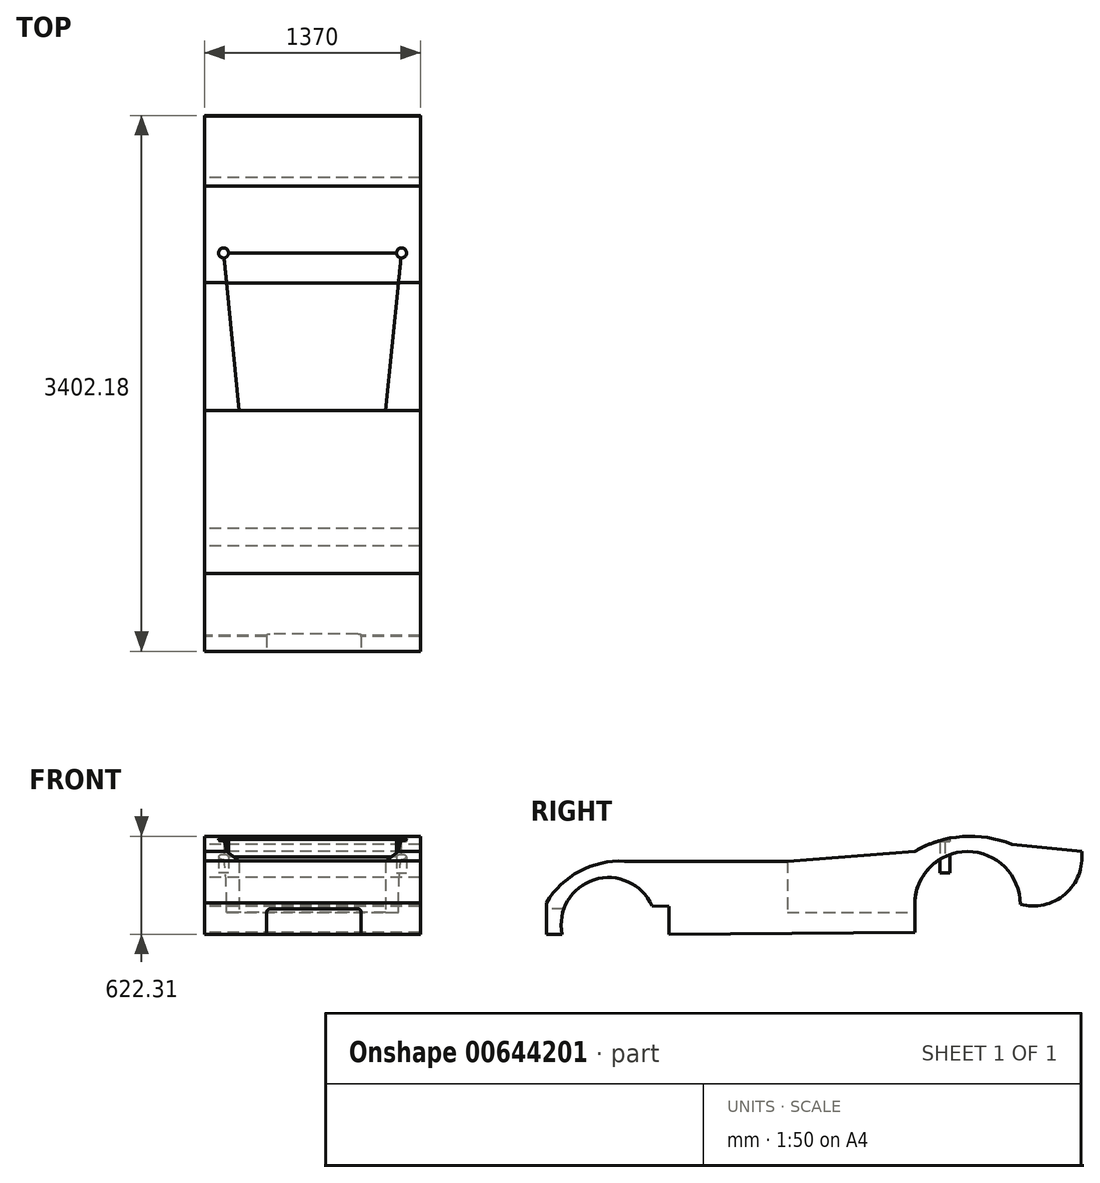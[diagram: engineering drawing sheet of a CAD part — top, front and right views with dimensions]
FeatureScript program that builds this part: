
annotation { "Feature Type Name" : "Feature", "Feature Type Description" : "" }
export const myFeature = defineFeature(function(context is Context, id is Id, definition is map)
    precondition{}
    {
        {
            var Q0;
            Q0=qCreatedBy(makeId("Right.planeOp"),FACE);
            var sketch = newSketch(context, id + "F0", { "sketchPlane" : qUnion([Q0])});
            skLineSegment(sketch, "E0", {"start": v(-1911.58, -464.58) * mm, "end": v(1488.42, -464.58) * mm, "construction": true});
            skLineSegment(sketch, "E1", {"start": v(1488.42, -464.58) * mm, "end": v(1488.42, 515.42) * mm, "construction": true});
            skLineSegment(sketch, "E2", {"start": v(-1911.58, -389.58) * mm, "end": v(-1811.58, -389.58) * mm});
            skLineSegment(sketch, "E3", {"start": v(-1131.58, -389.58) * mm, "end": v(428.38, -377.58) * mm});
            skLineSegment(sketch, "E4", {"start": v(-1131.58, -211.58) * mm, "end": v(428.38, -199.58) * mm});
            skLineSegment(sketch, "E5", {"start": v(428.38, -199.58) * mm, "end": v(428.38, -377.58) * mm});
            skLineSegment(sketch, "E6", {"start": v(-1131.58, -211.58) * mm, "end": v(-1131.58, -389.58) * mm});
            skArc(sketch, "E7", {"start": v(-1241.58, -209.76) * mm, "mid": v(-1607.46, -43.28) * mm, "end": v(-1811.58, -389.58) * mm});
            skLineSegment(sketch, "E8", {"start": v(-381.58, 74.2) * mm, "end": v(-1416.41, 74.2) * mm});
            skLineSegment(sketch, "E9", {"start": v(-1911.58, -389.58) * mm, "end": v(-1911.58, -189.58) * mm});
            skArc(sketch, "E10", {"start": v(-1416.41, 74.2) * mm, "mid": v(-1700.44, 10.73) * mm, "end": v(-1911.58, -189.58) * mm});
            skArc(sketch, "E11", {"start": v(1098.38, -199.58) * mm, "mid": v(763.38, 135.42) * mm, "end": v(428.38, -199.58) * mm});
            skLineSegment(sketch, "E12", {"start": v(-381.58, 74.2) * mm, "end": v(429.07, 137.05) * mm});
            skArc(sketch, "E13", {"start": v(1044.38, 181.8) * mm, "mid": v(731.52, 230.89) * mm, "end": v(429.07, 137.05) * mm});
            skArc(sketch, "E14", {"start": v(1098.38, -199.58) * mm, "mid": v(1382.86, -134.93) * mm, "end": v(1488.42, 137.05) * mm});
            skLineSegment(sketch, "E15", {"start": v(1488.42, 137.05) * mm, "end": v(1044.38, 181.8) * mm});
            skLineSegment(sketch, "E16", {"start": v(-1241.58, -209.76) * mm, "end": v(-1131.58, -211.58) * mm});
            skSolve(sketch);
        }
        {
            var Q0;
            Q0 = qSketchRegion(id + "F0", true);
            extrude(context, id + "F1", {"entities" : qUnion([Q0]), "depth" : 1370 * mm, "offsetDistance" : 25 * mm});
        }
        {
            var Q0;
            Q0=qCreatedBy(makeId("Top.planeOp"),FACE);
            var sketch = newSketch(context, id + "F2", { "sketchPlane" : qUnion([Q0])});
            skLineSegment(sketch, "E17", {"start": v(220, -381.58) * mm, "end": v(120, 618.42) * mm});
            skLineSegment(sketch, "E18", {"start": v(120, 618.42) * mm, "end": v(1250, 618.42) * mm});
            skLineSegment(sketch, "E19", {"start": v(1150, -381.58) * mm, "end": v(220, -381.58) * mm});
            skLineSegment(sketch, "E20", {"start": v(1150, -381.58) * mm, "end": v(1250, 618.42) * mm});
            skCircle(sketch, "E21", {"center": v(120, 618.42) * mm, "radius": 31.75 * mm});
            skCircle(sketch, "E22", {"center": v(1250, 618.42) * mm, "radius": 31.75 * mm});
            skSolve(sketch);
        }
        {
            var Q0;
            Q0 = qSketchRegion(id + "F2", true);
            extrude(context, id + "F3", {"entities" : qUnion([Q0]), "operationType" : NewBodyOperationType.REMOVE, "depth" : 350 * mm, "hasOffset" : true, "offsetDistance" : 200 * mm, "offsetOppositeDirection" : true, "hasSecondDirection" : true, "secondDirectionOppositeDirection" : true, "secondDirectionDepth" : 250 * mm});
        }
        {
            var Q0;
            Q0=makeQuery(id+"F1.opExtrude","SWEPT_FACE",FACE,{"disambiguationData":[OSD([sQuery(id+"F0.wireOp",EDGE,"E9")])]});
            var sketch = newSketch(context, id + "F4", { "sketchPlane" : qUnion([Q0])});
            skLineSegment(sketch, "E23.bottom", {"start": v(394.4, -389.58) * mm, "end": v(994.4, -389.58) * mm});
            skLineSegment(sketch, "E23.top", {"start": v(414.4, -229.58) * mm, "end": v(974.4, -229.58) * mm});
            skLineSegment(sketch, "E23.left", {"start": v(394.4, -389.58) * mm, "end": v(394.4, -249.58) * mm});
            skLineSegment(sketch, "E23.right", {"start": v(994.4, -389.58) * mm, "end": v(994.4, -249.58) * mm});
            skPoint(sketch, "E24.visualSharp", {"position": v(394.4, -229.58) * mm});
            skArc(sketch, "E24.filletArc", {"start": v(414.4, -229.58) * mm, "mid": v(400.27, -235.43) * mm, "end": v(394.4, -249.58) * mm});
            skPoint(sketch, "E25.visualSharp", {"position": v(994.4, -229.58) * mm});
            skArc(sketch, "E25.filletArc", {"start": v(994.4, -249.58) * mm, "mid": v(988.55, -235.43) * mm, "end": v(974.4, -229.58) * mm});
            skSolve(sketch);
        }
        {
            var Q0;
            Q0=makeQuery(id+"F4.imprint","IMPRINT",FACE,{"disambiguationData":[TD([[makeQuery(id+"F4.imprint","IMPRINT",EDGE,{"derivedFrom":sQuery(id+"F4.wireOp",EDGE,"E23.bottom")}),-1.0]])]});
            extrude(context, id + "F5", {"entities" : qUnion([Q0]), "operationType" : NewBodyOperationType.REMOVE, "oppositeDirection" : true, "depth" : 500 * mm, "offsetDistance" : 25 * mm});
        }
        {
            var Q0;
            {var subQ0=sQuery(id+"F2.wireOp",EDGE,"E18");var subQ1=sQuery(id+"F2.wireOp",EDGE,"E17");var subQ2=makeQuery(id+"F2.imprint","INTERSECT",VERTEX,{"derivedFrom":[subQ1,subQ0]});Q0=makeQuery(id+"F2.imprint","IMPRINT",FACE,{"disambiguationData":[TD([[makeQuery(id+"F2.imprint","IMPRINT",EDGE,{"disambiguationData":[TD([[subQ2,1.0]])],"derivedFrom":subQ1}),1.0]])]});}
            var Q1;
            {var subQ0=sQuery(id+"F2.wireOp",EDGE,"E18");var subQ1=sQuery(id+"F2.wireOp",EDGE,"E17");var subQ2=makeQuery(id+"F2.imprint","INTERSECT",VERTEX,{"derivedFrom":[subQ1,subQ0]});Q1=makeQuery(id+"F2.imprint","IMPRINT",FACE,{"disambiguationData":[TD([[makeQuery(id+"F2.imprint","IMPRINT",EDGE,{"disambiguationData":[TD([[subQ2,1.0]])],"derivedFrom":subQ1}),-1.0]])]});}
            var Q2;
            {var subQ0=sQuery(id+"F2.wireOp",EDGE,"E20");var subQ1=sQuery(id+"F2.wireOp",EDGE,"E18");var subQ2=makeQuery(id+"F2.imprint","INTERSECT",VERTEX,{"derivedFrom":[subQ1,subQ0]});Q2=makeQuery(id+"F2.imprint","IMPRINT",FACE,{"disambiguationData":[TD([[makeQuery(id+"F2.imprint","IMPRINT",EDGE,{"disambiguationData":[TD([[subQ2,1.0]])],"derivedFrom":subQ1}),-1.0]])]});}
            var Q3;
            {var subQ0=sQuery(id+"F2.wireOp",EDGE,"E20");var subQ1=sQuery(id+"F2.wireOp",EDGE,"E18");var subQ2=makeQuery(id+"F2.imprint","INTERSECT",VERTEX,{"derivedFrom":[subQ1,subQ0]});Q3=makeQuery(id+"F2.imprint","IMPRINT",FACE,{"disambiguationData":[TD([[makeQuery(id+"F2.imprint","IMPRINT",EDGE,{"disambiguationData":[TD([[subQ2,1.0]])],"derivedFrom":subQ1}),1.0]])]});}
            extrude(context, id + "F6", {"entities" : qUnion([Q0, Q1, Q2, Q3]), "operationType" : NewBodyOperationType.ADD, "depth" : 200 * mm, "offsetDistance" : 25 * mm});
        }
    });
